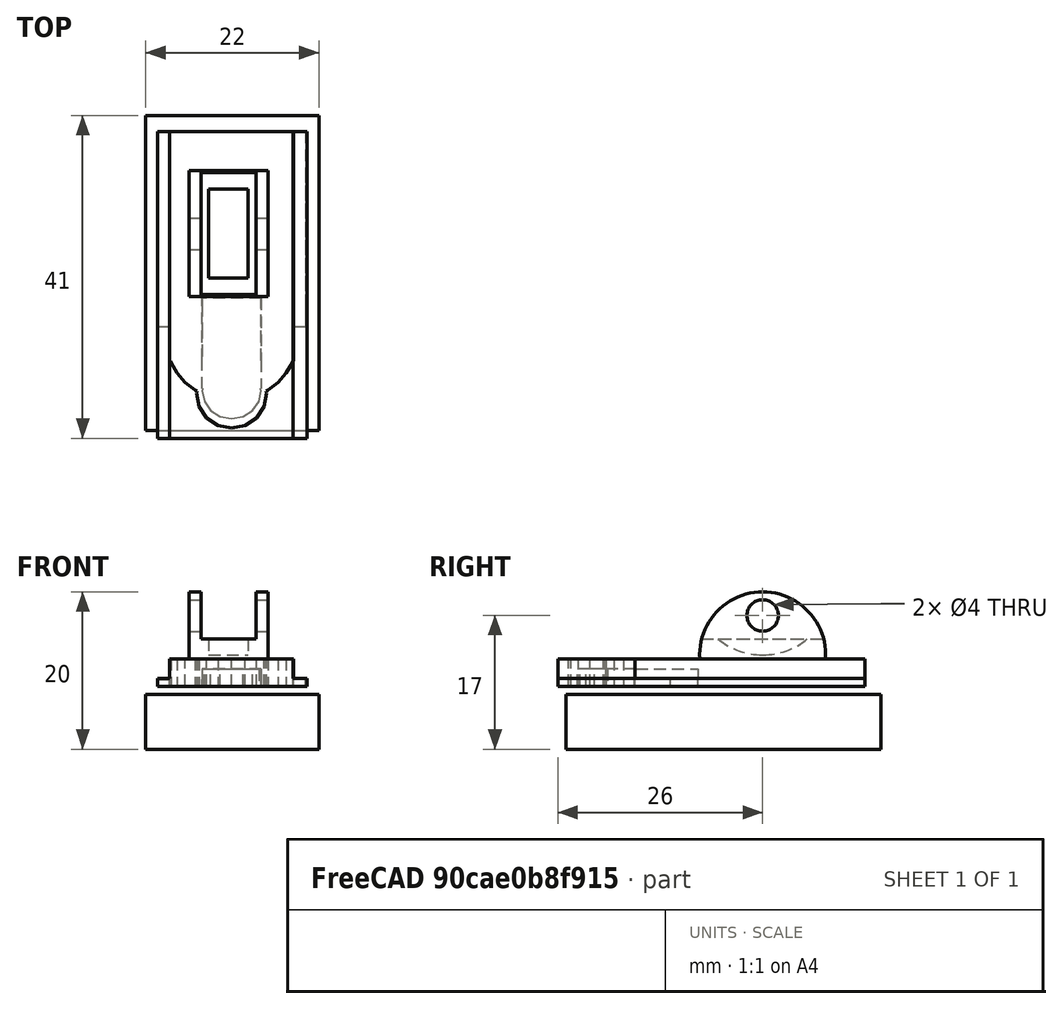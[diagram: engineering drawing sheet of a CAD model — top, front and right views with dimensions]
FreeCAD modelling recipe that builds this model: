
FCSTD DOCUMENT  (FreeCAD 0.15R4671 (Git))
Label: base_finished
License: All rights reserved
LicenseURL: http://en.wikipedia.org/wiki/All_rights_reserved
objects: Part::Box×5, App::FeaturePython×4, Part::Cut×4, Part::Cylinder×3, Part::MultiFuse×2, Part::Feature×1
note: 15 computed .brp shape members not serialized (recipe doc carries the construction recipe); baked Part::Feature solids carry a one-line shape summary decoded from their .brp

FEATURE [Part::Feature] Solid  label="Base"
  shape: bbox 18.8 x 37.7 x 3.5 mm, 49 faces (baked)
FEATURE [App::FeaturePython] Dimension  # Draft dimension (typed FeaturePython)
  Dimline = (-24.2999,-37,0)
  Direction = (0,0,0)
  Distance = 24.8
  End = (-21,-37,0)
  Normal = (0,0,1)
  Start = (-21,-61.8,0)
FEATURE [App::FeaturePython] Dimension001  # Draft dimension (typed FeaturePython)
  Dimline = (-19.5482,-29.7066,0)
  Direction = (0,0,0)
  Distance = 18.8
  End = (-21,-37,0)
  Normal = (0,0,1)
  Start = (-2.2,-37,0)
FEATURE [App::FeaturePython] Dimension002  # Draft dimension (typed FeaturePython)
  Dimline = (-7,-34,0)
  Direction = (0,0,0)
  Distance = 15.7
  End = (-3.75,-37,0)
  Normal = (0,0,1)
  Start = (-19.45,-37,0)
FEATURE [App::FeaturePython] Dimension003  # Draft dimension (typed FeaturePython)
  Dimline = (-24.5637,-27.4775,0)
  Direction = (0,0,0)
  Distance = 3.5
  End = (-19.45,-37,0)
  Normal = (0,0,1)
  Start = (-19.45,-37,3.5)
FEATURE [Part::Cylinder] Cylinder001  label="Cilindro001"
  Angle = 360
  Height = 10
  Placement = pos=(-17,-50,4) rot=(0,1,0;1.5708rad)
  Radius = 8
FEATURE [Part::MultiFuse] Fusion  label="base_con_cilindro"
  Shapes = -> [Solid,Cylinder001]
FEATURE [Part::Box] Box  label="Cubo"
  Height = 10
  Length = 20
  Placement = pos=(-19,-59,-10) rot=(0,0,1;0rad)
  Width = 17
FEATURE [Part::Cut] Cut  label="base_cilindro_solid"
  Base = -> Fusion
  Tool = -> Box
FEATURE [Part::Box] Box001  label="Cubo001"
  Height = 10
  Length = 7
  Placement = pos=(-15.5,-59,6) rot=(0,0,1;0rad)
  Width = 22
FEATURE [Part::Cut] Cut001
  Base = -> Cut
  Tool = -> Box001
FEATURE [Part::Cylinder] Cylinder002  label="Cilindro002"
  Angle = 360
  Height = 10
  Placement = pos=(-17,-50,9) rot=(0,1,0;1.5708rad)
  Radius = 2
FEATURE [Part::Cut] Cut002
  Base = -> Cut001
  Tool = -> Cylinder002
FEATURE [Part::Cylinder] Cylinder  label="Cilindro003"
  Angle = 360
  Height = 5
  Placement = pos=(-14.5,-50,13) rot=(0,1,0;1.5708rad)
  Radius = 9
FEATURE [Part::Cut] Cut003  label="base_finished"
  Base = -> Cut002
  Placement = pos=(21,62,0) rot=(0,0,1;0rad)
  Tool = -> Cylinder
FEATURE [Part::Box] Box002  label="Cubo002"
  Height = 7
  Length = 22
  Placement = pos=(-1.5,-13,-8) rot=(0,0,1;0rad)
  Width = 40
FEATURE [Part::Box] Box003  label="Cubo003"
  Height = 1
  Length = 19
  Placement = pos=(0,-14,0) rot=(0,0,1;0rad)
  Width = 39
FEATURE [Part::Box] Box004  label="Cubo004"
  Height = 3.5
  Length = 15.7
  Placement = pos=(1.5,-14,0) rot=(0,0,1;0rad)
  Width = 39
FEATURE [Part::MultiFuse] Fusion001
  Shapes = -> [Box003,Box004]
